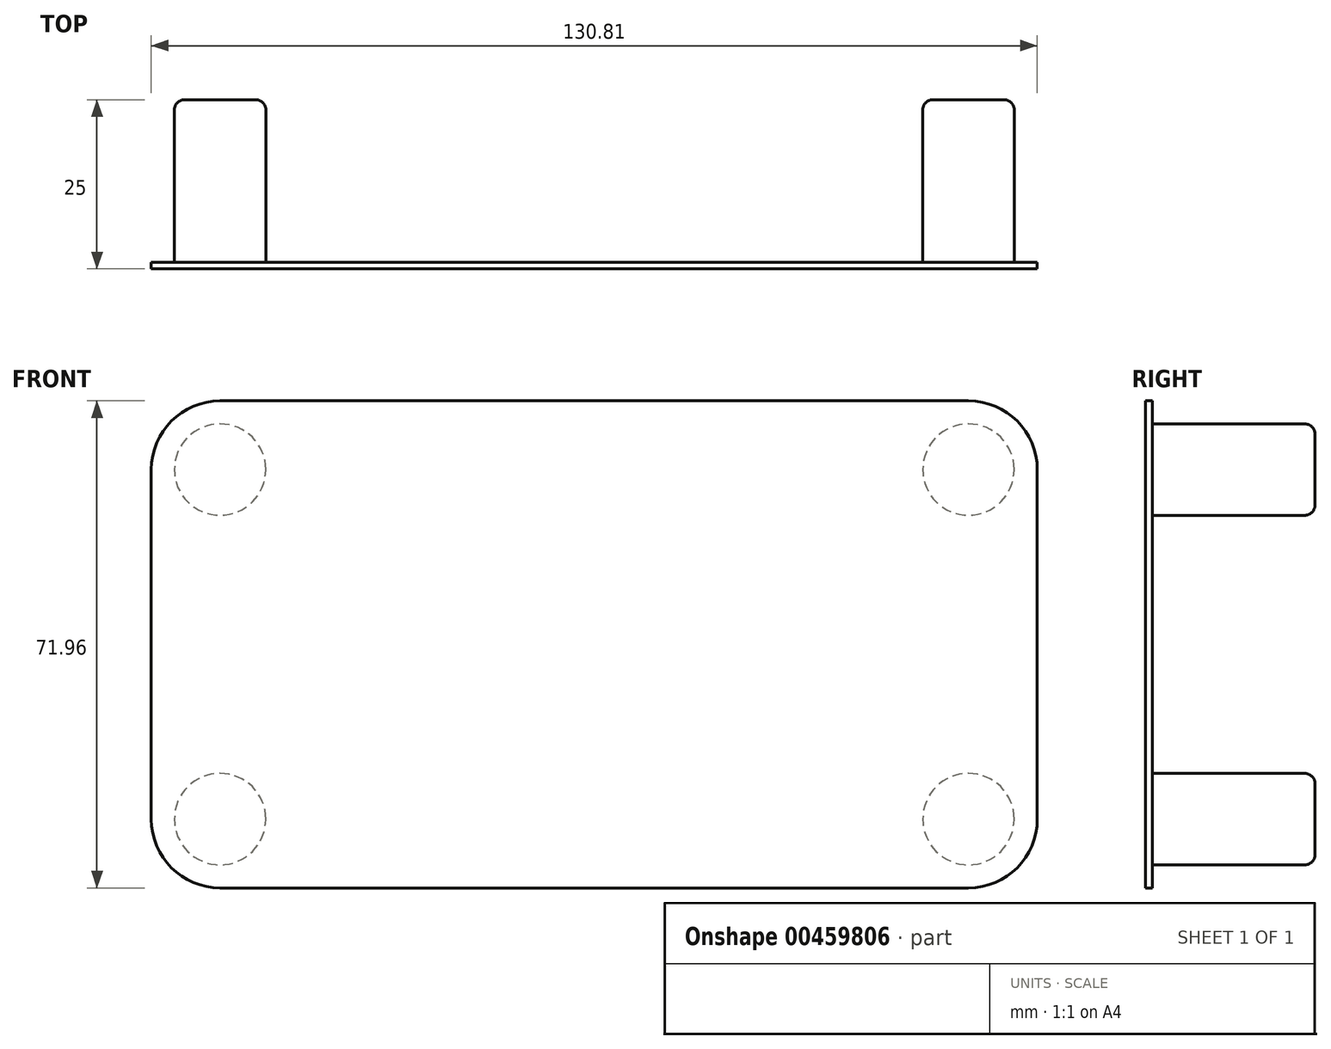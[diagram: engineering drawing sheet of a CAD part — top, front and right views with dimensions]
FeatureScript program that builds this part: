
annotation { "Feature Type Name" : "Feature", "Feature Type Description" : "" }
export const myFeature = defineFeature(function(context is Context, id is Id, definition is map)
    precondition{}
    {
        {
            var Q0;
            Q0=qCreatedBy(makeId("Front.planeOp"),FACE);
            var sketch = newSketch(context, id + "F0", { "sketchPlane" : qUnion([Q0])});
            skLineSegment(sketch, "E0.bottom", {"start": v(35.94, -21.69) * mm, "end": v(-74.55, -21.69) * mm});
            skLineSegment(sketch, "E0.top", {"start": v(35.94, 50.27) * mm, "end": v(-74.55, 50.27) * mm});
            skLineSegment(sketch, "E0.left", {"start": v(46.1, -11.53) * mm, "end": v(46.1, 40.11) * mm});
            skLineSegment(sketch, "E0.right", {"start": v(-84.7, -11.53) * mm, "end": v(-84.7, 40.11) * mm});
            skArc(sketch, "E1.filletArc", {"start": v(-74.55, 50.27) * mm, "mid": v(-81.73, 47.3) * mm, "end": v(-84.7, 40.11) * mm});
            skArc(sketch, "E2.filletArc", {"start": v(-84.7, -11.53) * mm, "mid": v(-81.73, -18.71) * mm, "end": v(-74.55, -21.69) * mm});
            skArc(sketch, "E3.filletArc", {"start": v(35.94, -21.69) * mm, "mid": v(43.13, -18.71) * mm, "end": v(46.1, -11.53) * mm});
            skArc(sketch, "E4.filletArc", {"start": v(46.1, 40.11) * mm, "mid": v(43.13, 47.3) * mm, "end": v(35.94, 50.27) * mm});
            skCircle(sketch, "E5", {"center": v(-74.55, 40.11) * mm, "radius": 6.75 * mm});
            skCircle(sketch, "E6", {"center": v(35.94, -11.53) * mm, "radius": 6.75 * mm});
            skCircle(sketch, "E7", {"center": v(35.94, 40.11) * mm, "radius": 6.75 * mm});
            skCircle(sketch, "E8", {"center": v(-74.55, -11.53) * mm, "radius": 6.75 * mm});
            skSolve(sketch);
        }
        {
            var Q0;
            Q0=makeQuery(id+"F0.imprint","IMPRINT",FACE,{"disambiguationData":[TD([[makeQuery(id+"F0.imprint","IMPRINT",EDGE,{"derivedFrom":sQuery(id+"F0.wireOp",EDGE,"E0.bottom")}),-1.0]])]});
            extrude(context, id + "F1", {"entities" : qUnion([Q0]), "oppositeDirection" : true, "depth" : 1 * mm});
        }
        {
            var Q0;
            Q0=makeQuery(id+"F0.imprint","IMPRINT",FACE,{"disambiguationData":[TD([[makeQuery(id+"F0.imprint","IMPRINT",EDGE,{"derivedFrom":sQuery(id+"F0.wireOp",EDGE,"E7")}),1.0]])]});
            var Q1;
            Q1=makeQuery(id+"F0.imprint","IMPRINT",FACE,{"disambiguationData":[TD([[makeQuery(id+"F0.imprint","IMPRINT",EDGE,{"derivedFrom":sQuery(id+"F0.wireOp",EDGE,"E6")}),1.0]])]});
            var Q2;
            Q2=makeQuery(id+"F0.imprint","IMPRINT",FACE,{"disambiguationData":[TD([[makeQuery(id+"F0.imprint","IMPRINT",EDGE,{"derivedFrom":sQuery(id+"F0.wireOp",EDGE,"E8")}),1.0]])]});
            var Q3;
            Q3=makeQuery(id+"F0.imprint","IMPRINT",FACE,{"disambiguationData":[TD([[makeQuery(id+"F0.imprint","IMPRINT",EDGE,{"derivedFrom":sQuery(id+"F0.wireOp",EDGE,"E5")}),1.0]])]});
            var Q4;
            Q4=makeQuery(id+"F1.opExtrude","SWEPT_FACE",FACE,{"disambiguationData":[OSD([sQuery(id+"F0.wireOp",EDGE,"E5")])]});
            extrude(context, id + "F2", {"entities" : qUnion([Q0, Q1, Q2, Q3]), "operationType" : NewBodyOperationType.ADD, "oppositeDirection" : true, "endBoundEntityFace" : qUnion([Q4]), "depth" : 25 * mm});
        }
        {
            var Q0;
            Q0=makeQuery(id+"F2.opExtrude","CAP_EDGE",EDGE,{"disambiguationData":[OSD([sQuery(id+"F0.wireOp",EDGE,"E5")])],"isStart":false});
            var Q1;
            Q1=makeQuery(id+"F2.opExtrude","CAP_EDGE",EDGE,{"disambiguationData":[OSD([sQuery(id+"F0.wireOp",EDGE,"E7")])],"isStart":false});
            var Q2;
            Q2=makeQuery(id+"F2.opExtrude","CAP_EDGE",EDGE,{"disambiguationData":[OSD([sQuery(id+"F0.wireOp",EDGE,"E6")])],"isStart":false});
            var Q3;
            Q3=makeQuery(id+"F2.opExtrude","CAP_EDGE",EDGE,{"disambiguationData":[OSD([sQuery(id+"F0.wireOp",EDGE,"E8")])],"isStart":false});
            fillet(context, id + "F3", {"entities" : qUnion([Q0, Q1, Q2, Q3]), "radius" : 1.5 * mm, "tangentPropagation" : true, "allowEdgeOverflow" : false});
        }
    });
